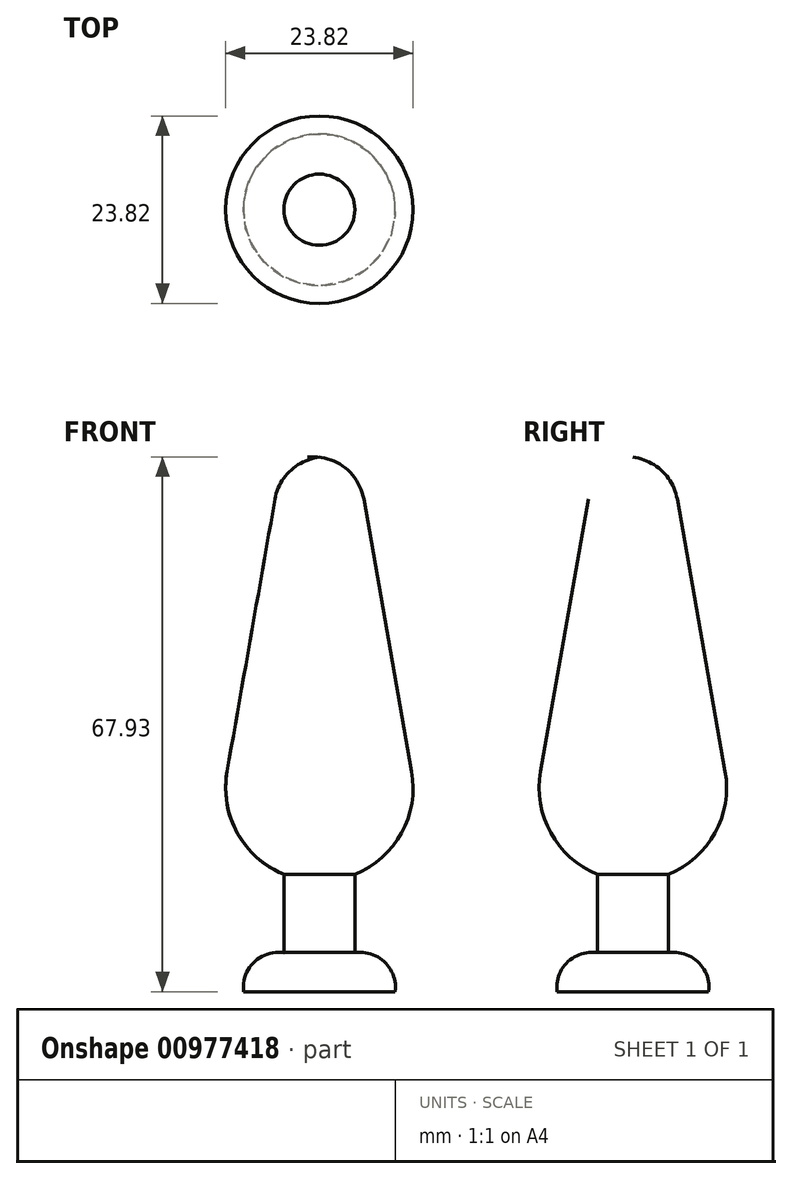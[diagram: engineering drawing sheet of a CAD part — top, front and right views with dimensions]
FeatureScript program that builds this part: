
annotation { "Feature Type Name" : "Feature", "Feature Type Description" : "" }
export const myFeature = defineFeature(function(context is Context, id is Id, definition is map)
    precondition{}
    {
        {
            var Q0;
            Q0=qCreatedBy(makeId("Front.planeOp"),FACE);
            var sketch = newSketch(context, id + "F0", { "sketchPlane" : qUnion([Q0])});
            skLineSegment(sketch, "E0", {"start": v(-5.64, 62.57) * mm, "end": v(-11.73, 27.98) * mm});
            skLineSegment(sketch, "E1", {"start": v(-4.51, 14.9) * mm, "end": v(-4.51, 4.93) * mm});
            skArc(sketch, "E2", {"start": v(-4.51, 4.93) * mm, "mid": v(-8.3, 3.75) * mm, "end": v(-9.63, 0) * mm});
            skArc(sketch, "E3", {"start": v(-11.73, 27.98) * mm, "mid": v(-10.43, 20.16) * mm, "end": v(-4.51, 14.9) * mm});
            skArc(sketch, "E4", {"start": v(0, 67.89) * mm, "mid": v(-3.7, 66.17) * mm, "end": v(-5.64, 62.57) * mm});
            skLineSegment(sketch, "E5", {"start": v(-9.63, 0) * mm, "end": v(0, 0) * mm});
            skLineSegment(sketch, "E6", {"start": v(0, 0) * mm, "end": v(0, 67.89) * mm});
            skSolve(sketch);
        }
        {
            var Q0;
            Q0 = qSketchRegion(id + "F0", true);
            var Q1;
            Q1=sQuery(id+"F0.wireOp",EDGE,"E6");
            revolve(context, id + "F1", {"surfaceOperationType" : NewSurfaceOperationType.NEW, "entities" : qUnion([Q0]), "axis" : qUnion([Q1]), "revolveType" : RevolveType.FULL});
        }
    });
